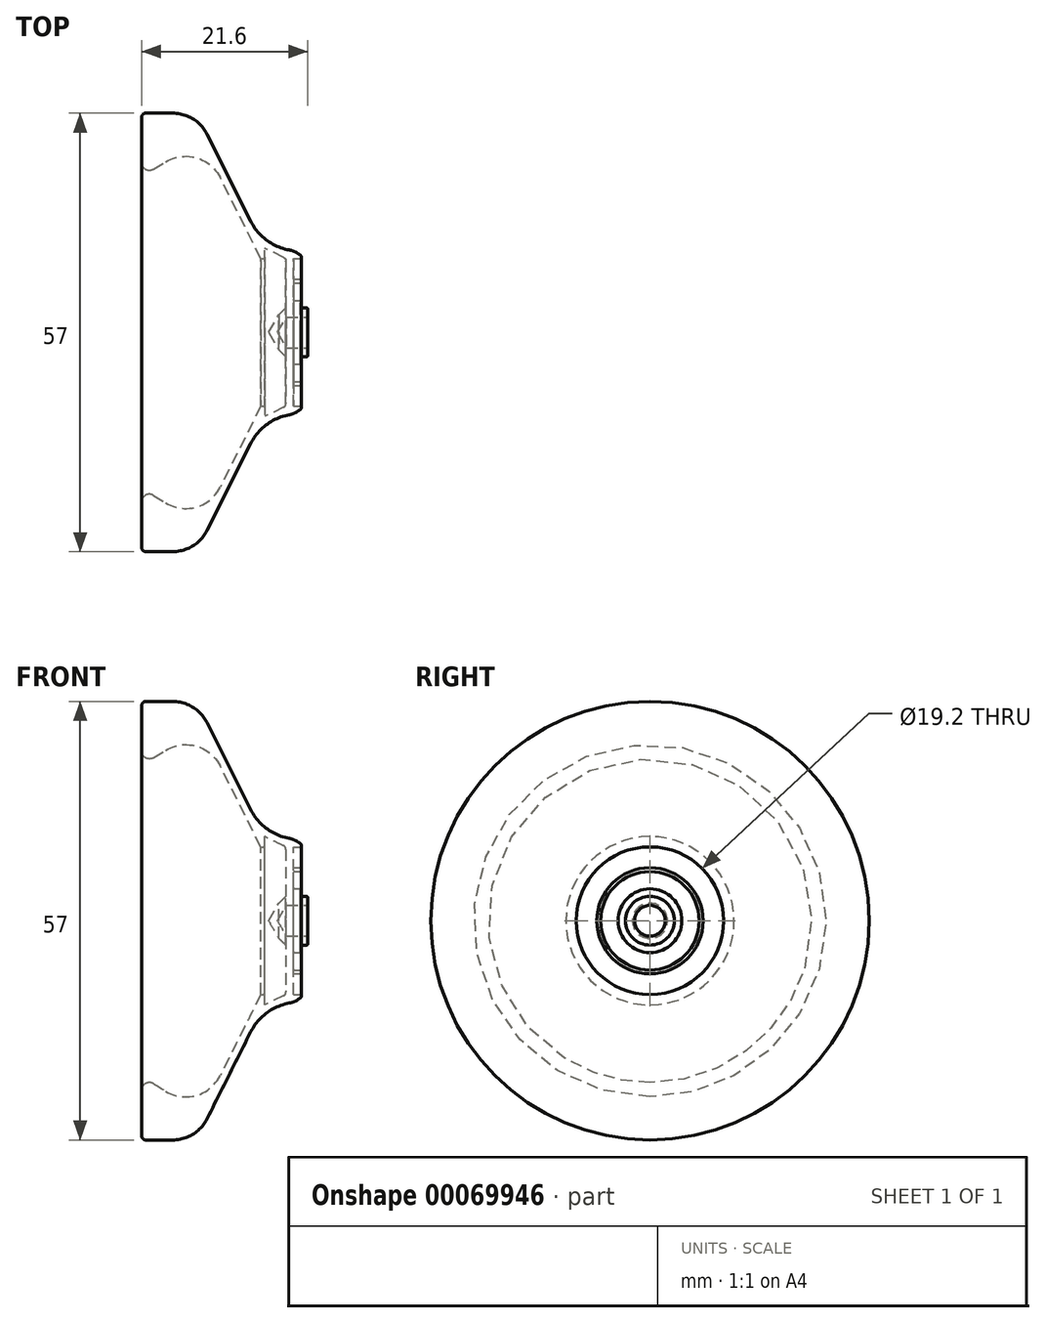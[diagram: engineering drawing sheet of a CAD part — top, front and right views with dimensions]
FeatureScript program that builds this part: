
annotation { "Feature Type Name" : "Feature", "Feature Type Description" : "" }
export const myFeature = defineFeature(function(context is Context, id is Id, definition is map)
    precondition{}
    {
        {
            var Q0;
            Q0=qCreatedBy(makeId("Front.planeOp"),FACE);
            var sketch = newSketch(context, id + "F0", { "sketchPlane" : qUnion([Q0])});
            skLineSegment(sketch, "E0", {"start": v(-1.4, 2) * mm, "end": v(-4.2, 2) * mm});
            skLineSegment(sketch, "E1", {"start": v(-4.2, 2) * mm, "end": v(-5.35, 0) * mm});
            skLineSegment(sketch, "E2", {"start": v(-5.35, 0) * mm, "end": v(-6.5, 0) * mm});
            skLineSegment(sketch, "E3", {"start": v(-6.5, 0) * mm, "end": v(-5.19, 2.29) * mm});
            skLineSegment(sketch, "E4", {"start": v(-7.2, 9.6) * mm, "end": v(-7.5, 9.6) * mm});
            skLineSegment(sketch, "E5", {"start": v(-7.5, 9.6) * mm, "end": v(-12.8, 20.14) * mm});
            skLineSegment(sketch, "E6", {"start": v(-23, 22.04) * mm, "end": v(-23, 28.5) * mm});
            skLineSegment(sketch, "E7", {"start": v(-23, 28.5) * mm, "end": v(-18.97, 28.5) * mm});
            skLineSegment(sketch, "E8", {"start": v(-1.4, 3.17) * mm, "end": v(-2.4, 3.17) * mm});
            skLineSegment(sketch, "E9", {"start": v(-2.4, 3.17) * mm, "end": v(-2.4, 4.15) * mm});
            skLineSegment(sketch, "E10", {"start": v(-2.4, 4.15) * mm, "end": v(-3.25, 4.15) * mm});
            skLineSegment(sketch, "E11", {"start": v(-3.25, 4.15) * mm, "end": v(-3.25, 6.4) * mm});
            skLineSegment(sketch, "E12", {"start": v(-3.25, 6.4) * mm, "end": v(-2.25, 6.4) * mm});
            skLineSegment(sketch, "E13", {"start": v(-2.25, 6.4) * mm, "end": v(-2.25, 6.9) * mm});
            skLineSegment(sketch, "E14", {"start": v(-2.25, 6.9) * mm, "end": v(-3.25, 6.9) * mm});
            skLineSegment(sketch, "E15", {"start": v(-3.25, 6.9) * mm, "end": v(-3.25, 9.6) * mm});
            skLineSegment(sketch, "E16", {"start": v(-3.25, 9.6) * mm, "end": v(-2.25, 9.6) * mm});
            skLineSegment(sketch, "E17", {"start": v(-2.25, 9.6) * mm, "end": v(-2.25, 10.6) * mm});
            skLineSegment(sketch, "E18", {"start": v(-1.4, 3.17) * mm, "end": v(-1.4, 2) * mm});
            skLineSegment(sketch, "E19", {"start": v(-2.1, 10.6) * mm, "end": v(-2.25, 10.6) * mm});
            skLineSegment(sketch, "E20", {"start": v(-4.25, 9.6) * mm, "end": v(-4.25, 3.17) * mm});
            skLineSegment(sketch, "E21", {"start": v(-4.25, 3.17) * mm, "end": v(-5.19, 2.29) * mm});
            skLineSegment(sketch, "E22", {"start": v(-2.25, 10.6) * mm, "end": v(-2.58, 10.6) * mm});
            skLineSegment(sketch, "E23", {"start": v(-14.5, 25.74) * mm, "end": v(-8.83, 14.46) * mm});
            skPoint(sketch, "E24.visualSharp", {"position": v(-6.9, 10.6) * mm});
            skArc(sketch, "E24.filletArc", {"start": v(-8.83, 14.46) * mm, "mid": v(-6.25, 11.64) * mm, "end": v(-2.58, 10.6) * mm});
            skPoint(sketch, "E25.visualSharp", {"position": v(-15.88, 28.5) * mm});
            skArc(sketch, "E25.filletArc", {"start": v(-14.5, 25.74) * mm, "mid": v(-16.34, 27.76) * mm, "end": v(-18.97, 28.5) * mm});
            skLineSegment(sketch, "E26", {"start": v(-21.48, 21.19) * mm, "end": v(-19.9, 22.16) * mm});
            skPoint(sketch, "E27.visualSharp", {"position": v(-15.25, 25.02) * mm});
            skArc(sketch, "E27.filletArc", {"start": v(-12.8, 20.14) * mm, "mid": v(-15.9, 22.71) * mm, "end": v(-19.9, 22.16) * mm});
            skPoint(sketch, "E28.visualSharp", {"position": v(-23, 20.25) * mm});
            skArc(sketch, "E28.filletArc", {"start": v(-23, 22.04) * mm, "mid": v(-22.49, 21.16) * mm, "end": v(-21.48, 21.19) * mm});
            skLineSegment(sketch, "E29", {"start": v(-7, 9.8) * mm, "end": v(-7, 10.94) * mm});
            skLineSegment(sketch, "E30", {"start": v(-7, 10.94) * mm, "end": v(-4.25, 9.6) * mm});
            skPoint(sketch, "E31.visualSharp", {"position": v(-7, 9.6) * mm});
            skArc(sketch, "E31.filletArc", {"start": v(-7.2, 9.6) * mm, "mid": v(-7.07, 9.66) * mm, "end": v(-7, 9.8) * mm});
            skSolve(sketch);
        }
        {
            var Q0;
            Q0=qSketchRegion(id+"F0",true);
            var Q1;
            Q1=sQuery(id+"F0.wireOp",EDGE,"E2");
            revolve(context, id + "F1", {"entities" : qUnion([Q0]), "axis" : qUnion([Q1]), "revolveType" : RevolveType.FULL});
        }
        {
            var Q0;
            Q0=makeQuery(id+"F1.opRevolve","SWEPT_EDGE",EDGE,{"disambiguationData":[OSD([sQuery(id+"F0.wireOp",EDGE,"E17"),sQuery(id+"F0.wireOp",EDGE,"E22")])]});
            chamfer(context, id + "F2", {"entities" : qUnion([Q0]), "chamferType" : ChamferType.TWO_OFFSETS, "width1" : 0.7 * mm, "oppositeDirection" : false, "width2" : 0.8 * mm, "tangentPropagation" : true});
        }
        {
            var Q0;
            Q0=makeQuery(id+"F2.opChamfer","BLEND_EDGE",EDGE,{"blendedFrom":[makeQuery(id+"F1.opRevolve","SWEPT_EDGE",EDGE,{"disambiguationData":[OSD([sQuery(id+"F0.wireOp",EDGE,"E17"),sQuery(id+"F0.wireOp",EDGE,"E22")])]}),makeQuery(id+"F1.opRevolve","SWEPT_FACE",FACE,{"disambiguationData":[OSD([sQuery(id+"F0.wireOp",EDGE,"E24.filletArc")])]})],"blendedInto":[makeQuery(id+"F1.opRevolve","SWEPT_FACE",FACE,{"disambiguationData":[OSD([sQuery(id+"F0.wireOp",EDGE,"E24.filletArc")])]})]});
            fillet(context, id + "F3", {"entities" : qUnion([Q0]), "radius" : 3 * mm, "tangentPropagation" : true, "allowEdgeOverflow" : false});
        }
        {
            var Q0;
            {var subQ0=sQuery(id+"F0.wireOp",EDGE,"E17");Q0=makeQuery(id+"F2.opChamfer","BLEND_EDGE",EDGE,{"blendedFrom":[makeQuery(id+"F1.opRevolve","SWEPT_EDGE",EDGE,{"disambiguationData":[OSD([subQ0,sQuery(id+"F0.wireOp",EDGE,"E22")])]}),makeQuery(id+"F1.opRevolve","SWEPT_FACE",FACE,{"disambiguationData":[OSD([subQ0])]})],"blendedInto":[makeQuery(id+"F1.opRevolve","SWEPT_FACE",FACE,{"disambiguationData":[OSD([subQ0])]})]});}
            fillet(context, id + "F4", {"entities" : qUnion([Q0]), "radius" : 0.2 * mm, "tangentPropagation" : true, "allowEdgeOverflow" : false});
        }
        {
            var Q0;
            Q0=makeQuery(id+"F1.opRevolve","SWEPT_EDGE",EDGE,{"disambiguationData":[OSD([sQuery(id+"F0.wireOp",EDGE,"E9"),sQuery(id+"F0.wireOp",EDGE,"E10")])]});
            var Q1;
            Q1=makeQuery(id+"F1.opRevolve","SWEPT_EDGE",EDGE,{"disambiguationData":[OSD([sQuery(id+"F0.wireOp",EDGE,"E10"),sQuery(id+"F0.wireOp",EDGE,"E11")])]});
            var Q2;
            Q2=makeQuery(id+"F1.opRevolve","SWEPT_EDGE",EDGE,{"disambiguationData":[OSD([sQuery(id+"F0.wireOp",EDGE,"E12"),sQuery(id+"F0.wireOp",EDGE,"E13")])]});
            var Q3;
            Q3=makeQuery(id+"F1.opRevolve","SWEPT_EDGE",EDGE,{"disambiguationData":[OSD([sQuery(id+"F0.wireOp",EDGE,"E13"),sQuery(id+"F0.wireOp",EDGE,"E14")])]});
            var Q4;
            Q4=makeQuery(id+"F1.opRevolve","SWEPT_EDGE",EDGE,{"disambiguationData":[OSD([sQuery(id+"F0.wireOp",EDGE,"E16"),sQuery(id+"F0.wireOp",EDGE,"E17")])]});
            var Q5;
            Q5=makeQuery(id+"F1.opRevolve","SWEPT_EDGE",EDGE,{"disambiguationData":[OSD([sQuery(id+"F0.wireOp",EDGE,"E11"),sQuery(id+"F0.wireOp",EDGE,"E12")])]});
            var Q6;
            Q6=makeQuery(id+"F1.opRevolve","SWEPT_EDGE",EDGE,{"disambiguationData":[OSD([sQuery(id+"F0.wireOp",EDGE,"E8"),sQuery(id+"F0.wireOp",EDGE,"E9")])]});
            fillet(context, id + "F5", {"entities" : qUnion([Q0, Q1, Q2, Q3, Q4, Q5, Q6]), "radius" : 0.1 * mm, "tangentPropagation" : true, "allowEdgeOverflow" : false});
        }
        {
            var Q0;
            Q0=makeQuery(id+"F1.opRevolve","SWEPT_EDGE",EDGE,{"disambiguationData":[OSD([sQuery(id+"F0.wireOp",EDGE,"E8"),sQuery(id+"F0.wireOp",EDGE,"E18")])]});
            fillet(context, id + "F6", {"entities" : qUnion([Q0]), "radius" : 0.2 * mm, "tangentPropagation" : true, "allowEdgeOverflow" : false});
        }
        {
            var Q0;
            Q0=makeQuery(id+"F1.opRevolve","SWEPT_EDGE",EDGE,{"disambiguationData":[OSD([sQuery(id+"F0.wireOp",EDGE,"E6"),sQuery(id+"F0.wireOp",EDGE,"E7")])]});
            fillet(context, id + "F7", {"entities" : qUnion([Q0]), "radius" : 0.5 * mm, "tangentPropagation" : true, "allowEdgeOverflow" : false});
        }
        {
            var Q0;
            Q0=makeQuery(id+"F1.opRevolve","SWEPT_EDGE",EDGE,{"disambiguationData":[OSD([sQuery(id+"F0.wireOp",EDGE,"E20"),sQuery(id+"F0.wireOp",EDGE,"E30")])]});
            fillet(context, id + "F8", {"entities" : qUnion([Q0]), "radius" : 0.5 * mm, "tangentPropagation" : true, "allowEdgeOverflow" : false});
        }
    });
